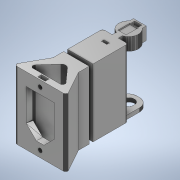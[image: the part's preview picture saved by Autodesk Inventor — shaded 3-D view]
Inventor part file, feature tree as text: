
AUTODESK INVENTOR PART (.ipt)
format: ipt  version: 2021 (Build 250183000, 183)  size: 3,782,144 bytes
history: mixed  units: in
note: dims shown in document units (in); Inventor stores cm internally (conversion verified against a paired STEP export)
features: extrude x6, sketch x6, move_body x5, other x4, plane x2, split x1, boolean_combine x1, imported_body x1
ambient origin geometry x8: Origin, YZ Plane, XZ Plane, XY Plane, X Axis, Y Axis, Z Axis, Center Point
bodies: Solid1 (imported_parasolid), Solid4 (imported_parasolid), Solid5 (imported_parasolid), Solid2 (imported_parasolid), Solid3 (imported_parasolid)
feature tree (26):
  other  "PenSlider"
  other  "MeshFeature1"
  plane  "Work Plane1"
  split  "Split2"
  move_body  "Move Body1"
  extrude  "Extrusion1"  TaperAngle=0.0deg  [1 undecoded]
  extrude  "Extrusion2"  Depth=0.4941in
  extrude  "Extrusion3"  Depth=0.5925in
  extrude  "Extrusion4"  Depth=1.2992in
  plane  "Work Plane2"
  extrude  "Extrusion5"  Depth=0.1969in TaperAngle=0.0deg
  extrude  "Extrusion6"  Depth=0.3937in
  other  "Servo-Rotation"
  other  "Servo-Static"
  boolean_combine  "Combine1"
  move_body  "Move Body2"
  move_body  "Move Body3"
  move_body  "Move Body4"
  move_body  "Move Body5"
  sketch  "Sketch1"  dims[d0=-0.0689in d1=0.0in d2=0.0in d3=-1.378in]
  sketch  "Sketch2"  dims[d4=0.9016in d5=0.4941in]
  sketch  "Sketch3"  dims[d6=0.1459in d9=0.5925in]
  sketch  "Sketch4"  dims[d10=0.6693in d11=0.0in d12=1.2992in]
  sketch  "Sketch5"  dims[d13=0.3445in d14=0.0in d15=0.1969in d16=0.0in]
  sketch  "Sketch6"  dims[d17=1.2677in d18=0.4843in d19=1.0827in d20=0.3346in d21=0.1907in d22=0.1272in d23=0.0in d24=0.2362in d25=0.0787in d26=0.1673in d27=0.0in d28=0.0in d29=0.0984in d30=0.1969in d31=0.1272in d32=0.0in d33=90.0deg d34=0.7764in d35=-0.2736in d36=1.6922in d37=0.0in d38=0.0in d39=0.3937in d40=0.0in d41=0.0in d42=-0.315in]
  imported_body  NMx_Import_Brep_tag  [imported B-rep: ~1903 faces, bbox_mm=[40.0, 53.000002, 78.240726]]
note: 1 required parameter value undecoded (feature->parameter linkage not recoverable at this tier; creation-order binding heuristic only, values carry confidence <= 0.55)
